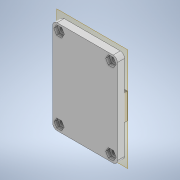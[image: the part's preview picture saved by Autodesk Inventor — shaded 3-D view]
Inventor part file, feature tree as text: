
AUTODESK INVENTOR PART (.ipt)
format: ipt  version: 2021.2 (Build 252289000, 289)  size: 214,016 bytes
history: native  units: mm
features: other x6, extrude x5, sketch x5, reference x3
ambient origin geometry x8: Origin, YZ Plane, XZ Plane, XY Plane, X Axis, Y Axis, Z Axis, Center Point
bodies: Body1 (feature_tree)
feature tree (19):
  other  "Твердое тело1"
  other  "РабПлоскость1"
  extrude  "Выдавливание1"  Depth=4.0mm TaperAngle=0.0deg
  sketch  "Эскиз2"
  extrude  "Выдавливание2"  Depth=6.3mm
  extrude  "Выдавливание3"  Depth=1.0mm TaperAngle=0.0deg
  extrude  "Выдавливание4"  Depth=1.0mm TaperAngle=0.0deg
  extrude  "Выдавливание5"  Depth=40.5mm
  sketch  "Эскиз1"
  reference  "Ссылка1"
  sketch  "Эскиз3"
  sketch  "Эскиз4"
  sketch  "Эскиз5"
  reference  "Ссылка2"
  reference  "Ссылка3"
  other  "Сборка1"
  other  "level1_up:1"
  other  "plate:1"
  other  "level3_up:1"
